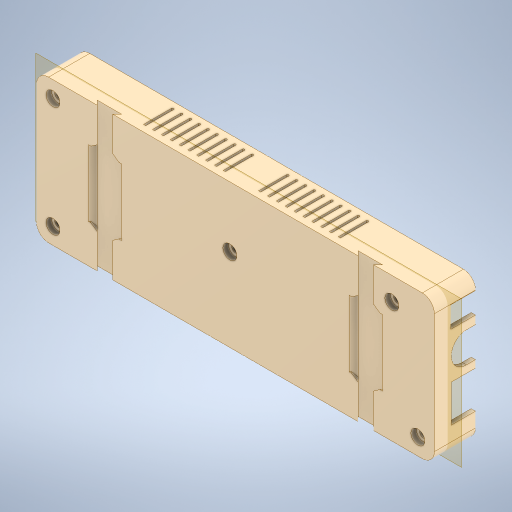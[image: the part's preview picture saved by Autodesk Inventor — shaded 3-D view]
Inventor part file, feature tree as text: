
AUTODESK INVENTOR PART (.ipt)
format: ipt  version: 2024.3 (Build 283343000, 343)  size: 910,848 bytes
history: native  units: in
note: dims shown in document units (in); Inventor stores cm internally (conversion verified against a paired STEP export)
features: reference x59, sketch x16, extrude x15, other x15, plane x5, chamfer x5, projected_geometry x2, hole x1
ambient origin geometry x8: Origin, YZ Plane, XZ Plane, XY Plane, X Axis, Y Axis, Z Axis, Center Point
bodies: Solid1 (feature_tree)
feature tree (118):
  plane  "Work Plane1"
  sketch  "Sketch1"  dims[d0=0.0197in d1=1.0in d2=0.0in]
  plane  "Work Plane2"
  extrude  "Extrusion1"  Depth=0.0197in TaperAngle=0.0deg
  extrude  "Extrusion2"  Depth=0.1181in TaperAngle=0.0deg
  extrude  "Extrusion3"  Depth=0.0118in
  sketch  "Sketch4"  dims[d9=0.0118in d10=0.0118in]
  plane  "Work Plane7"
  extrude  "Extrusion4"  Depth=0.0118in
  extrude  "Extrusion5"  Depth=0.0118in
  extrude  "Extrusion6"  Depth=0.0118in
  sketch  "Sketch7"  dims[d15=0.0118in d16=0.0118in]
  plane  "Work Plane4"
  extrude  "Extrusion7"  Depth=0.0118in
  extrude  "Extrusion8"  Depth=0.0118in
  hole  "Hole1"  [1 undecoded]
  extrude  "Extrusion11"  Depth=0.0118in
  extrude  "Extrusion9"  Depth=0.1181in
  extrude  "Extrusion10"  Depth=1.0in TaperAngle=0.0deg
  chamfer  "Chamfer1"  Distance=0.58in
  chamfer  "Chamfer3"  Distance=0.58in
  chamfer  "Chamfer4"  Distance=0.0787in
  extrude  "Extrusion12"  Depth=0.0787in
  extrude  "Extrusion13"  Depth=0.1575in
  sketch  "Sketch16"  dims[d42=0.134in d43=0.75in d44=0.248in d45=0.1in d46=90.0deg d47=1.0in d48=0.8108in]
  plane  "Work Plane8"
  extrude  "Extrusion14"  Depth=0.0394in TaperAngle=0.0deg
  extrude  "Extrusion15"  Depth=0.1575in
  chamfer  "Chamfer5"  Distance=0.1575in
  chamfer  "Chamfer6"  Distance=0.0787in
  reference  "Reference1"
  reference  "Reference2"
  reference  "Reference3"
  reference  "Reference4"
  reference  "Reference5"
  reference  "Reference6"
  reference  "Reference7"
  reference  "Reference8"
  reference  "Reference9"
  reference  "Reference10"
  sketch  "Sketch2"  dims[d3=0.1181in d4=0.0in d5=0.1181in d6=0.0in]
  projected_geometry  "Projected Loop1"
  sketch  "Sketch3"  dims[d7=0.0118in d8=0.0118in]
  projected_geometry  "Projected Loop2"
  reference  "Reference11"
  reference  "Reference12"
  reference  "Reference13"
  reference  "Reference14"
  reference  "Reference15"
  reference  "Reference16"
  reference  "Reference17"
  reference  "Reference18"
  reference  "Reference19"
  reference  "Reference20"
  reference  "Reference21"
  reference  "Reference22"
  reference  "Reference23"
  reference  "Reference24"
  reference  "Reference25"
  reference  "Reference26"
  reference  "Reference27"
  reference  "Reference28"
  sketch  "Sketch5"  dims[d11=0.0118in d12=0.0118in]
  reference  "Reference29"
  reference  "Reference30"
  reference  "Reference31"
  reference  "Reference32"
  reference  "Reference33"
  sketch  "Sketch6"  dims[d13=0.0118in d14=0.0118in]
  reference  "Reference34"
  reference  "Reference35"
  reference  "Reference38"
  sketch  "Sketch9"  dims[d17=0.0118in d18=0.0118in]
  reference  "Reference39"
  reference  "Reference40"
  reference  "Reference41"
  reference  "Reference42"
  reference  "Reference43"
  reference  "Reference44"
  reference  "Reference45"
  reference  "Reference46"
  reference  "Reference47"
  sketch  "Sketch10"  dims[d19=0.0118in d20=0.0118in]
  reference  "Reference48"
  reference  "Reference49"
  reference  "Reference50"
  reference  "Reference51"
  reference  "Reference52"
  reference  "Reference53"
  reference  "Reference54"
  reference  "Reference55"
  sketch  "Sketch11"  dims[d21=0.0118in d22=0.0118in]
  sketch  "Sketch12"  dims[d23=0.1181in d24=0.0in d26=0.0157in]
  sketch  "Sketch13"  dims[d30=1.0in d31=0.0in d33=1.0in d34=0.0in]
  reference  "Reference56"
  reference  "Reference57"
  reference  "Reference58"
  reference  "Reference59"
  reference  "Reference60"
  reference  "Reference61"
  sketch  "Sketch14"  dims[d35=0.0079in d36=0.58in d37=0.0in]
  sketch  "Sketch15"  dims[d39=0.4331in d40=0.58in d41=0.0in]
  sketch  "Sketch17"  dims[d49=0.315in d50=0.0787in d51=0.0787in d52=0.1575in d53=0.0394in d54=0.0in d55=0.1575in d56=0.1575in d57=0.0787in d58=0.0394in d59=0.0in d60=0.0394in d61=0.125in d62=45.0deg d63=0.0079in d64=0.1181in d65=0.0in d66=0.0787in d71=0.27in d72=0.0079in d73=0.0787in d75=0.0787in d76=0.0787in d77=45.0deg d78=0.0118in d79=0.0118in d80=0.0197in d81=0.0787in d82=45.0deg d83=0.1181in d84=0.1181in d85=0.0394in d86=0.315in d87=0.0197in d88=2.3622in d90=0.1575in d91=0.3937in d93=0.3937in d95=1.0in d96=0.0in d97=1.1811in d99=0.1575in d100=0.3937in d102=0.3937in d104=0.0394in d105=0.2756in d106=0.7874in d107=0.0in d108=0.0in d109=0.0394in d110=0.0197in d111=0.1181in d112=0.1181in d113=1.5748in d114=3.937in d116=0.1575in d117=0.3937in d119=0.3937in d121=0.3937in d122=0.0in d123=3.937in d125=0.1575in d126=0.3937in d128=0.3937in d130=0.5906in d131=0.5906in d132=0.3937in d133=0.0in d134=0.0787in d135=0.0787in d136=45.0deg d137=0.0787in d138=0.0787in d139=45.0deg]
  other  "<userpath>\Dropbox\elec\Mechanical\DCBuddyV2\PCB\_TOP_Design.iam"
  other  "_TOP_Design.iam"
  other  "dcbuddy_v2:1"
  other  "dcbuddy_v2_BOARD:1"
  other  "CUI-PJ-002A_V_CMP-167-0003-2:2"
  other  "FP-43045-0802-MFG_CMP-002-00102-1:1"
  other  "CUI-PJ-002A_V_CMP-167-0003-2:3"
  other  "CUI-PJ-002A_V_CMP-167-0003-2:4"
  other  "CUI-PJ-002A_V_CMP-167-0003-2:5"
  other  "CUI-PJ-002A_V_CMP-167-0003-2:6"
  other  "CUI-PJ-002A_V_CMP-167-0003-2:7"
  other  "CUI-PJ-002A_V_CMP-167-0003-2:8"
  other  "CUI-PJ-002A_V_CMP-167-0003-2:1"
  other  "PD40S_CMP-167-0005-1:1"
  other  "AMPHENOL_10155435-00011LF_CMP-243-000000-3:1"
note: 1 required parameter value undecoded (feature->parameter linkage not recoverable at this tier; creation-order binding heuristic only, values carry confidence <= 0.55)
